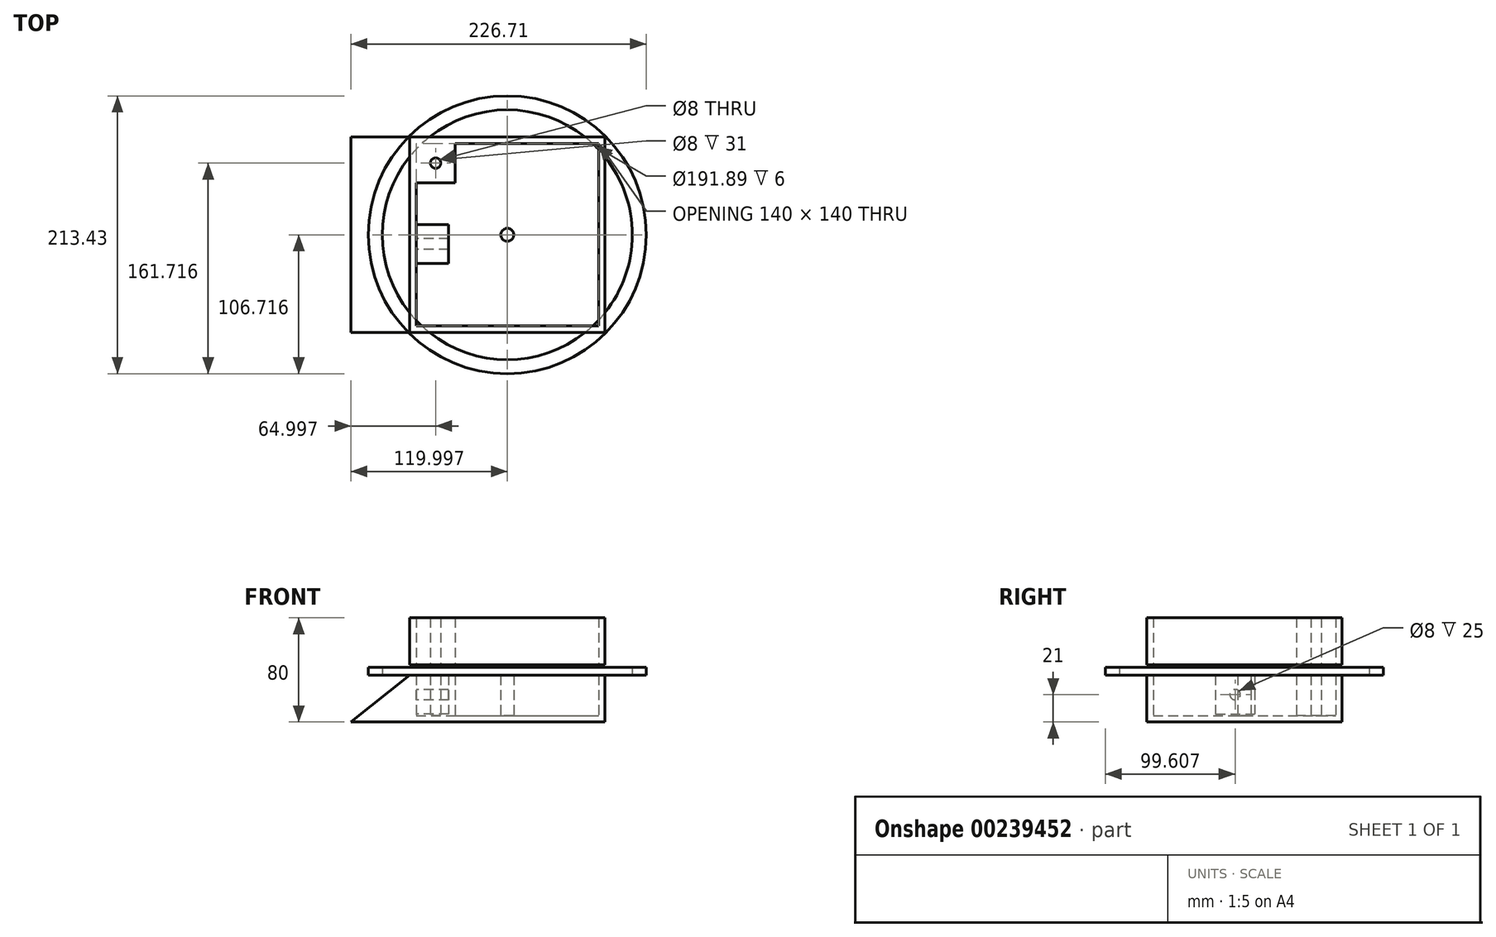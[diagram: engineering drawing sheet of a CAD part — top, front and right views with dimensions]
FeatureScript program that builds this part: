
annotation { "Feature Type Name" : "Feature", "Feature Type Description" : "" }
export const myFeature = defineFeature(function(context is Context, id is Id, definition is map)
    precondition{}
    {
        {
            var Q0;
            Q0=qCreatedBy(makeId("Top.planeOp"),FACE);
            var sketch = newSketch(context, id + "F0", { "sketchPlane" : qUnion([Q0])});
            skLineSegment(sketch, "E0.bottom", {"start": v(-90.82, -56.9) * mm, "end": v(59.18, -56.9) * mm});
            skLineSegment(sketch, "E0.top", {"start": v(-90.82, 93.1) * mm, "end": v(59.18, 93.1) * mm});
            skLineSegment(sketch, "E0.left", {"start": v(-90.82, -56.9) * mm, "end": v(-90.82, 93.1) * mm});
            skLineSegment(sketch, "E0.right", {"start": v(59.18, -56.9) * mm, "end": v(59.18, 93.1) * mm});
            skSolve(sketch);
        }
        {
            var Q0;
            Q0=makeQuery(id+"F0.imprint","IMPRINT",FACE,{"disambiguationData":[TD([[makeQuery(id+"F0.imprint","IMPRINT",EDGE,{"derivedFrom":sQuery(id+"F0.wireOp",EDGE,"E0.bottom")}),1.0]])]});
            extrude(context, id + "F1", {"entities" : qUnion([Q0]), "depth" : 80 * mm});
        }
        {
            var Q0;
            Q0=makeQuery(id+"F1.opExtrude","CAP_FACE",FACE,{"disambiguationData":[OSD([sQuery(id+"F0.wireOp",EDGE,"E0.bottom"),sQuery(id+"F0.wireOp",EDGE,"E0.top"),sQuery(id+"F0.wireOp",EDGE,"E0.left"),sQuery(id+"F0.wireOp",EDGE,"E0.right")])],"isStart":false});
            shell(context, id + "F2", {"entities" : qUnion([Q0]), "thickness" : 5 * mm});
        }
        {
            var Q0;
            Q0=makeQuery(id+"F2.opShell","OFFSET_FACE",FACE,{"disambiguationData":[OSD([sQuery(id+"F0.wireOp",EDGE,"E0.bottom"),sQuery(id+"F0.wireOp",EDGE,"E0.top"),sQuery(id+"F0.wireOp",EDGE,"E0.left"),sQuery(id+"F0.wireOp",EDGE,"E0.right")])]});
            var sketch = newSketch(context, id + "F3", { "sketchPlane" : qUnion([Q0])});
            skLineSegment(sketch, "E1.bottom", {"start": v(-85.82, 88.1) * mm, "end": v(-55.82, 88.1) * mm});
            skLineSegment(sketch, "E1.top", {"start": v(-85.82, 58.1) * mm, "end": v(-55.82, 58.1) * mm});
            skLineSegment(sketch, "E1.left", {"start": v(-85.82, 88.1) * mm, "end": v(-85.82, 58.1) * mm});
            skLineSegment(sketch, "E1.right", {"start": v(-55.82, 88.1) * mm, "end": v(-55.82, 58.1) * mm});
            skCircle(sketch, "E2", {"center": v(-70.82, 73.1) * mm, "radius": 4 * mm});
            skSolve(sketch);
        }
        {
            var Q0;
            Q0=makeQuery(id+"F3.imprint","IMPRINT",FACE,{"disambiguationData":[TD([[makeQuery(id+"F3.imprint","IMPRINT",EDGE,{"derivedFrom":sQuery(id+"F3.wireOp",EDGE,"E1.bottom")}),-1.0]])]});
            extrude(context, id + "F4", {"entities" : qUnion([Q0]), "operationType" : NewBodyOperationType.ADD, "depth" : 75 * mm});
        }
        {
            var Q0;
            Q0=makeQuery(id+"F1.opExtrude","SWEPT_FACE",FACE,{"disambiguationData":[OSD([sQuery(id+"F0.wireOp",EDGE,"E0.bottom")])]});
            var sketch = newSketch(context, id + "F5", { "sketchPlane" : qUnion([Q0])});
            skLineSegment(sketch, "E3.bottom", {"start": v(-90.82, 44) * mm, "end": v(59.18, 44) * mm});
            skLineSegment(sketch, "E3.top", {"start": v(-90.82, 36) * mm, "end": v(59.18, 36) * mm});
            skLineSegment(sketch, "E3.left", {"start": v(-90.82, 44) * mm, "end": v(-90.82, 36) * mm});
            skLineSegment(sketch, "E3.right", {"start": v(59.18, 44) * mm, "end": v(59.18, 36) * mm});
            skSolve(sketch);
        }
        {
            var Q0;
            Q0=makeQuery(id+"F5.imprint","IMPRINT",FACE,{"disambiguationData":[TD([[makeQuery(id+"F5.imprint","IMPRINT",EDGE,{"derivedFrom":sQuery(id+"F5.wireOp",EDGE,"E3.bottom")}),-1.0]])]});
            extrude(context, id + "F6", {"entities" : qUnion([Q0]), "operationType" : NewBodyOperationType.REMOVE, "oppositeDirection" : true, "depth" : 150 * mm});
        }
        {
            var Q0;
            {var subQ1=sQuery(id+"F0.wireOp",EDGE,"E0.left");Q0=makeQuery(id+"F6.boolean.opBoolean","SPLIT",FACE,{"disambiguationData":[TD([makeQuery(id+"F6.opExtrude","SWEPT_FACE",FACE,{"disambiguationData":[OSD([sQuery(id+"F5.wireOp",EDGE,"E3.top")])]})])],"derivedFrom":makeQuery(id+"F2.opShell","OFFSET_FACE",FACE,{"disambiguationData":[OSD([subQ1])]})});}
            var sketch = newSketch(context, id + "F7", { "sketchPlane" : qUnion([Q0])});
            skLineSegment(sketch, "E4.bottom", {"start": v(-4.01, 36) * mm, "end": v(25.99, 36) * mm});
            skLineSegment(sketch, "E4.top", {"start": v(-4.01, 6) * mm, "end": v(25.99, 6) * mm});
            skLineSegment(sketch, "E4.left", {"start": v(-4.01, 36) * mm, "end": v(-4.01, 6) * mm});
            skLineSegment(sketch, "E4.right", {"start": v(25.99, 36) * mm, "end": v(25.99, 6) * mm});
            skSolve(sketch);
        }
        {
            var Q0;
            Q0=makeQuery(id+"F7.imprint","IMPRINT",FACE,{"disambiguationData":[TD([[makeQuery(id+"F7.imprint","IMPRINT",EDGE,{"derivedFrom":sQuery(id+"F7.wireOp",EDGE,"E4.bottom")}),1.0]])]});
            var sketch = newSketch(context, id + "F8", { "sketchPlane" : qUnion([Q0])});
            skCircle(sketch, "E5", {"center": v(10.99, 21) * mm, "radius": 4 * mm});
            skSolve(sketch);
        }
        {
            var Q0;
            Q0=makeQuery(id+"F8.imprint","IMPRINT",FACE,{"disambiguationData":[TD([[makeQuery(id+"F8.imprint","IMPRINT",EDGE,{"derivedFrom":sQuery(id+"F8.wireOp",EDGE,"E5")}),-1.0]])]});
            extrude(context, id + "F9", {"entities" : qUnion([Q0]), "operationType" : NewBodyOperationType.ADD, "depth" : 25 * mm});
        }
        {
            var Q0;
            {var subQ2=sQuery(id+"F0.wireOp",EDGE,"E0.bottom");Q0=makeQuery(id+"F6.boolean.opBoolean","SPLIT",FACE,{"disambiguationData":[TD([makeQuery(id+"F6.opExtrude","SWEPT_FACE",FACE,{"disambiguationData":[OSD([sQuery(id+"F5.wireOp",EDGE,"E3.top")])]})])],"derivedFrom":makeQuery(id+"F1.opExtrude","SWEPT_FACE",FACE,{"disambiguationData":[OSD([subQ2])]})});}
            var sketch = newSketch(context, id + "F10", { "sketchPlane" : qUnion([Q0])});
            skLineSegment(sketch, "E6", {"start": v(-90.82, 0) * mm, "end": v(-135.82, 0) * mm});
            skLineSegment(sketch, "E7", {"start": v(-135.82, 0) * mm, "end": v(-90.82, 36) * mm});
            skSolve(sketch);
        }
        {
            var Q0;
            Q0 = qSketchRegion(id + "F10", true);
            var Q1;
            Q1=makeQuery(id+"F10.imprint","IMPRINT",FACE,{"disambiguationData":[TD([[makeQuery(id+"F10.imprint","IMPRINT",EDGE,{"derivedFrom":sQuery(id+"F10.wireOp",EDGE,"E6")}),-1.0]])]});
            extrude(context, id + "F11", {"entities" : qUnion([Q0, Q1]), "operationType" : NewBodyOperationType.ADD, "oppositeDirection" : true, "depth" : 150 * mm});
        }
        {
            var Q0;
            {var subQ0=sQuery(id+"F0.wireOp",EDGE,"E0.right");var subQ1=sQuery(id+"F0.wireOp",EDGE,"E0.left");var subQ2=sQuery(id+"F0.wireOp",EDGE,"E0.top");var subQ3=sQuery(id+"F0.wireOp",EDGE,"E0.bottom");Q0=makeQuery(id+"F4.boolean.opBoolean","SPLIT",FACE,{"disambiguationData":[TD([makeQuery(id+"F2.opShell","OFFSET_FACE",FACE,{"disambiguationData":[OSD([subQ3])]})])],"derivedFrom":makeQuery(id+"F2.opShell","OFFSET_FACE",FACE,{"disambiguationData":[OSD([subQ3,subQ2,subQ1,subQ0])]})});}
            var sketch = newSketch(context, id + "F12", { "sketchPlane" : qUnion([Q0])});
            skCircle(sketch, "E8", {"center": v(-15.82, 18.1) * mm, "radius": 5 * mm});
            skSolve(sketch);
        }
        {
            var Q0;
            Q0 = qSketchRegion(id + "F12", true);
            extrude(context, id + "F13", {"entities" : qUnion([Q0]), "operationType" : NewBodyOperationType.ADD, "depth" : 31 * mm});
        }
        {
            var Q0;
            Q0=makeQuery(id+"F13.opExtrude","CAP_FACE",FACE,{"disambiguationData":[OSD([sQuery(id+"F12.wireOp",EDGE,"E8")])],"isStart":false});
            var sketch = newSketch(context, id + "F14", { "sketchPlane" : qUnion([Q0])});
            skCircle(sketch, "E9", {"center": v(-15.82, 18.1) * mm, "radius": 95.94 * mm});
            skCircle(sketch, "E10", {"center": v(-15.82, 18.1) * mm, "radius": 106.71 * mm});
            skSolve(sketch);
        }
        {
            var Q0;
            Q0=makeQuery(id+"F14.imprint","IMPRINT",FACE,{"disambiguationData":[TD([[makeQuery(id+"F14.imprint","IMPRINT",EDGE,{"derivedFrom":sQuery(id+"F14.wireOp",EDGE,"E9")}),-1.0]])]});
            extrude(context, id + "F15", {"entities" : qUnion([Q0]), "operationType" : NewBodyOperationType.ADD, "depth" : 6 * mm});
        }
        {
            var Q0;
            {var subQ0=sQuery(id+"F10.wireOp",EDGE,"E7");var subQ1=sQuery(id+"F10.wireOp",EDGE,"E6");var subQ2=sQuery(id+"F0.wireOp",EDGE,"E0.left");var subQ3=sQuery(id+"F0.wireOp",EDGE,"E0.bottom");var subQ4=sQuery(id+"F14.wireOp",EDGE,"E10");var subQ5=sQuery(id+"F14.wireOp",EDGE,"E9");Q0=makeQuery(id+"F15.boolean.opBoolean","SPLIT",FACE,{"disambiguationData":[TD([makeQuery(id+"F1.opExtrude","SWEPT_FACE",FACE,{"disambiguationData":[OSD([subQ3])]}),makeQuery(id+"F1.opExtrude","SWEPT_FACE",FACE,{"disambiguationData":[OSD([sQuery(id+"F0.wireOp",EDGE,"E0.top")])]}),makeQuery(id+"F1.opExtrude","SWEPT_FACE",FACE,{"disambiguationData":[OSD([sQuery(id+"F0.wireOp",EDGE,"E0.right")])]}),makeQuery(id+"F6.boolean.opBoolean","COPY",FACE,{"derivedFrom":makeQuery(id+"F6.opExtrude","SWEPT_FACE",FACE,{"disambiguationData":[OSD([sQuery(id+"F5.wireOp",EDGE,"E3.top")])]})}),makeQuery(id+"F9.opExtrude","SWEPT_FACE",FACE,{"disambiguationData":[OSD([sQuery(id+"F7.wireOp",EDGE,"E4.bottom")])]}),makeQuery(id+"F11.opExtrude","CAP_FACE",FACE,{"disambiguationData":[OSD([subQ3,subQ2,subQ1,subQ0])],"isStart":true}),makeQuery(id+"F11.opExtrude","CAP_FACE",FACE,{"disambiguationData":[OSD([subQ3,subQ2,subQ1,subQ0])],"isStart":false}),makeQuery(id+"F11.opExtrude","SWEPT_FACE",FACE,{"disambiguationData":[OSD([subQ0])]}),makeQuery(id+"F15.opExtrude","SWEPT_FACE",FACE,{"disambiguationData":[OSD([subQ5])]}),makeQuery(id+"F15.opExtrude","SWEPT_FACE",FACE,{"disambiguationData":[OSD([subQ4])]})])],"derivedFrom":makeQuery(id+"F15.opExtrude","CAP_FACE",FACE,{"disambiguationData":[OSD([subQ5,subQ4])],"isStart":true})});}
            extrude(context, id + "F16", {"entities" : qUnion([Q0]), "operationType" : NewBodyOperationType.ADD, "oppositeDirection" : true, "depth" : 1 * mm});
        }
        {
            var Q0;
            {var subQ0=sQuery(id+"F10.wireOp",EDGE,"E7");var subQ1=sQuery(id+"F10.wireOp",EDGE,"E6");var subQ2=sQuery(id+"F0.wireOp",EDGE,"E0.left");var subQ3=sQuery(id+"F0.wireOp",EDGE,"E0.bottom");var subQ4=sQuery(id+"F14.wireOp",EDGE,"E10");var subQ5=sQuery(id+"F14.wireOp",EDGE,"E9");Q0=makeQuery(id+"F15.boolean.opBoolean","SPLIT",FACE,{"disambiguationData":[TD([makeQuery(id+"F1.opExtrude","SWEPT_FACE",FACE,{"disambiguationData":[OSD([subQ3])]}),makeQuery(id+"F1.opExtrude","SWEPT_FACE",FACE,{"disambiguationData":[OSD([sQuery(id+"F0.wireOp",EDGE,"E0.top")])]}),makeQuery(id+"F1.opExtrude","SWEPT_FACE",FACE,{"disambiguationData":[OSD([sQuery(id+"F0.wireOp",EDGE,"E0.right")])]}),makeQuery(id+"F6.boolean.opBoolean","COPY",FACE,{"derivedFrom":makeQuery(id+"F6.opExtrude","SWEPT_FACE",FACE,{"disambiguationData":[OSD([sQuery(id+"F5.wireOp",EDGE,"E3.top")])]})}),makeQuery(id+"F9.opExtrude","SWEPT_FACE",FACE,{"disambiguationData":[OSD([sQuery(id+"F7.wireOp",EDGE,"E4.bottom")])]}),makeQuery(id+"F11.opExtrude","CAP_FACE",FACE,{"disambiguationData":[OSD([subQ3,subQ2,subQ1,subQ0])],"isStart":true}),makeQuery(id+"F11.opExtrude","CAP_FACE",FACE,{"disambiguationData":[OSD([subQ3,subQ2,subQ1,subQ0])],"isStart":false}),makeQuery(id+"F11.opExtrude","SWEPT_FACE",FACE,{"disambiguationData":[OSD([subQ0])]}),makeQuery(id+"F15.opExtrude","SWEPT_FACE",FACE,{"disambiguationData":[OSD([subQ5])]}),makeQuery(id+"F15.opExtrude","SWEPT_FACE",FACE,{"disambiguationData":[OSD([subQ4])]})])],"derivedFrom":makeQuery(id+"F15.opExtrude","CAP_FACE",FACE,{"disambiguationData":[OSD([subQ5,subQ4])],"isStart":true})});}
            extrude(context, id + "F17", {"entities" : qUnion([Q0]), "operationType" : NewBodyOperationType.ADD, "oppositeDirection" : true, "depth" : 2 * mm});
        }
    });
